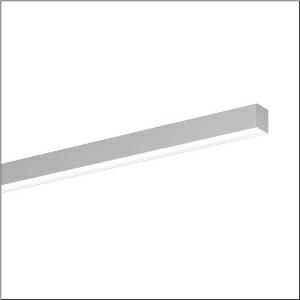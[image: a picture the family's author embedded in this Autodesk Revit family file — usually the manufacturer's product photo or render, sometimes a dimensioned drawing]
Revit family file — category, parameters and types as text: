
# Revit family: silica_r__21_51mx20db42sb_cda5
name_source: partatom
category: Lighting Fixtures
units: mm (PartAtom-declared; Revit-internal decimal feet)

## family parameters
Cut with Voids When Loaded = No
Host = Face
Light Source = No
Part Type = Normal
Room Calculation Point = No
Round Connector Dimension = Use Diameter
Shared = No

## types (1)
- --- (1 x LED, 3000 lm, 19 W, 4000K)
    Apparent Load = 19 VA
    CIE Flux Codes = 48 79 96 100 100
    Color Rendering = 80
    Color Temperature = 4000K
    Default Elevation = 1800 mm
    Description = Silica® 21, office luminaire, primary optical cover: cover, of PMMA, opal, light emission: direct distribution, primary light characteristic: symmetric, installation type: surface-mounted, LED, rated luminous flux: 3.000lm, luminous efficacy: 158lm/W, light colour: 840, colour temperature: 4000K, control gear: DALI 2, with terminal, 3+2-pole, max. 2.5mm², mains connection: 220..240V, AC, 50/60Hz, rated input power: 19W, luminaire housing, of aluminium, metallic grey (RAL 9006), length: 1.504mm, width: 53mm, height: 53mm, protection rating (complete): IP20, insulation class (complete): insulation class I (protective earthing), certification: CE, permissible operating ambient temperature: 0..+35°C, standard: EN 50419, packaging unit: 1 piece
    Height = 53 mm
    Lamp = 1 x LED
    Lamp Light Flux = 3000 lm
    Lamp Power = 19 W
    Lamp count = 1
    Length = 1504 mm
    Luminous efficacy = 158 lm/W
    Manufacturer = Siteco
    ModVariant = No
    Model = 51MX20DB42SB
    Mounting Place = Ceiling
    Mounting Type = Surface mounted
    Number of Poles = 1
    OnlyDefault = Yes
    Power Factor = 1
    Product Name = Silica® 21
    Product group = office luminaire | ceiling mounted
    ProductGroupID = 302
    Protection Class = Protection class I
    Protection Degree = IP 20
    RLX_Detail_Level = 1
    RLX_Emergency_Light_Flux = 0 lm
    RLX_Emergency_Type = 0
    RLX_Emergency_Type_DB = No
    RlxData = <blob elided: 26265 chars, md5=7958e324>
    Socket = socket
    Standby Power = 0 W
    System Light Flux = 3000 lm
    System Power = 19 W
    Type Comments = factory setting: luminous flux: 100 % | dim-lin: 254 | 218 mA
    Type Image = l_1335933.jpg
    URL = http://relux.com
    VarID = @adj_118010
    Voltage = 0 V
    Weight = 0.00 kg
    Width = 53 mm

## geometry (parser evidence)
native form markers: Blend x4, Sweep x9
no freeform markers — native parametric forms only
